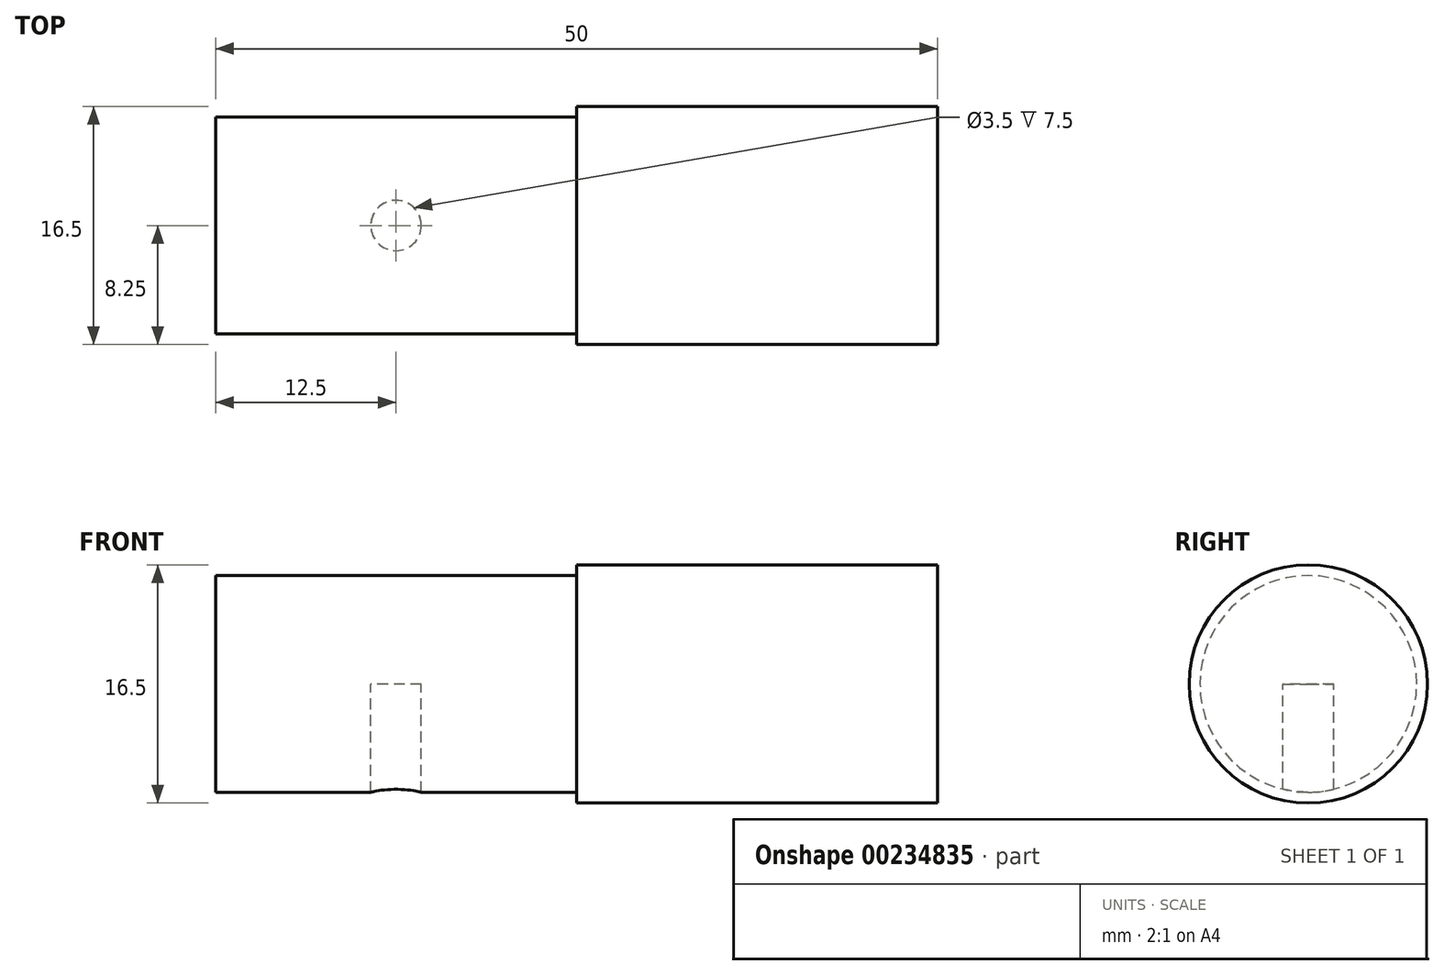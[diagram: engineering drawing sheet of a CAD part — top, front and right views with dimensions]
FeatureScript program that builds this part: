
annotation { "Feature Type Name" : "Feature", "Feature Type Description" : "" }
export const myFeature = defineFeature(function(context is Context, id is Id, definition is map)
    precondition{}
    {
        {
            var Q0;
            Q0=qCreatedBy(makeId("Right.planeOp"),FACE);
            var sketch = newSketch(context, id + "F0", { "sketchPlane" : qUnion([Q0])});
            skCircle(sketch, "E0", {"center": v(0, 0) * mm, "radius": 7.5 * mm});
            skSolve(sketch);
        }
        {
            var Q0;
            Q0 = qSketchRegion(id + "F0", true);
            extrude(context, id + "F1", {"entities" : qUnion([Q0]), "depth" : 25 * mm});
        }
        {
            var Q0;
            Q0=makeQuery(id+"F1.opExtrude","CAP_FACE",FACE,{"disambiguationData":[OSD([sQuery(id+"F0.wireOp",EDGE,"E0")])],"isStart":false});
            var sketch = newSketch(context, id + "F2", { "sketchPlane" : qUnion([Q0])});
            skCircle(sketch, "E1", {"center": v(0, 0) * mm, "radius": 8.25 * mm});
            skSolve(sketch);
        }
        {
            var Q0;
            Q0 = qSketchRegion(id + "F2", true);
            extrude(context, id + "F3", {"entities" : qUnion([Q0]), "operationType" : NewBodyOperationType.ADD, "depth" : 25 * mm});
        }
        {
            var Q0;
            Q0=qCreatedBy(makeId("Top.planeOp"),FACE);
            var sketch = newSketch(context, id + "F4", { "sketchPlane" : qUnion([Q0])});
            skCircle(sketch, "E2", {"center": v(12.5, 0) * mm, "radius": 1.75 * mm});
            skSolve(sketch);
        }
        {
            var Q0;
            Q0 = qSketchRegion(id + "F4", true);
            extrude(context, id + "F5", {"entities" : qUnion([Q0]), "operationType" : NewBodyOperationType.REMOVE, "oppositeDirection" : true, "depth" : 25 * mm});
        }
    });
